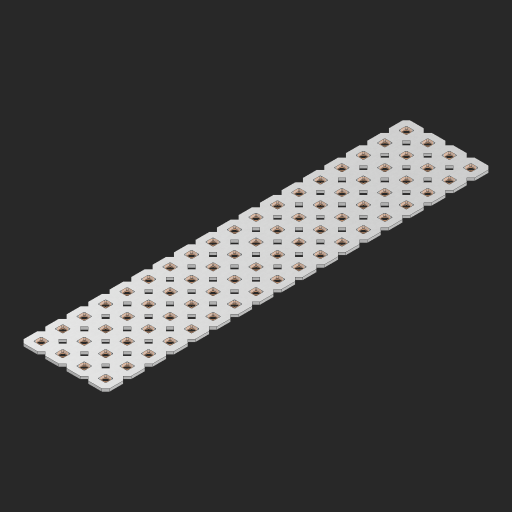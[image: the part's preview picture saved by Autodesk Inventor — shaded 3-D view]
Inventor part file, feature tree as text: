
AUTODESK INVENTOR PART (.ipt)
format: ipt  version: 2023 (Build 270158000, 158)  size: 1,118,720 bytes
history: native  units: in
note: dims shown in document units (in); Inventor stores cm internally (conversion verified against a paired STEP export)
features: other x73, extrude x71, sketch x2, pattern_linear x1
ambient origin geometry x8: Origin, YZ Plane, XZ Plane, XY Plane, X Axis, Y Axis, Z Axis, Center Point
bodies: Solid1 (feature_tree), Body (feature_tree)
feature tree (147):
  pattern_linear  "Rectangular Pattern1"  Spacing1=0.09in  [1 undecoded]
  sketch  "Sketch1"  dims[d1=0.5in]
  sketch  "Sketch2"  dims[d2=0.182in d3=0.09in d4=0.09in d5=0.09in d6=0.09in d7=0.09in d8=0.09in d9=0.09in d10=0.09in d11=0.02in d13=0.0in d14=0.172in d15=0.0625in d16=0.0in d19=0.5in d22=0.5in]
  other  "Srf1"
  other  "Srf126"
  other  "Srf127"
  other  "Srf128"
  other  "Srf129"
  other  "Srf130"
  other  "Srf131"
  other  "Srf250"
  other  "Srf251"
  other  "Srf252"
  other  "Srf253"
  other  "Srf254"
  other  "Srf255"
  other  "Srf256"
  other  "Srf257"
  other  "Srf258"
  other  "Srf259"
  other  "Srf260"
  other  "Srf268"
  other  "Srf269"
  other  "Srf270"
  other  "Srf271"
  other  "Srf272"
  other  "Srf273"
  other  "Srf274"
  other  "Srf275"
  other  "Srf276"
  other  "Srf277"
  other  "Srf278"
  other  "Srf279"
  other  "Srf280"
  other  "Srf281"
  other  "Srf282"
  other  "Srf283"
  other  "Srf284"
  other  "Srf285"
  other  "Srf293"
  other  "Srf294"
  other  "Srf295"
  other  "Srf296"
  other  "Srf297"
  other  "Srf298"
  other  "Srf299"
  other  "Srf300"
  other  "Srf301"
  other  "Srf302"
  other  "Srf303"
  other  "Srf304"
  other  "Srf305"
  other  "Srf306"
  other  "Srf307"
  other  "Srf308"
  other  "Srf309"
  other  "Srf310"
  other  "Srf318"
  other  "Srf319"
  other  "Srf320"
  other  "Srf321"
  other  "Srf322"
  other  "Srf323"
  other  "Srf324"
  other  "Srf325"
  other  "Srf326"
  other  "Srf327"
  other  "Srf328"
  other  "Srf329"
  other  "Srf330"
  other  "Srf331"
  other  "Srf332"
  other  "Srf333"
  other  "Srf334"
  other  "Srf335"
  other  "Circle"
  extrude  "ExtrusionSrf126"  Depth=0.09in
  extrude  "ExtrusionSrf127"  Depth=0.09in
  extrude  "ExtrusionSrf128"  Depth=0.09in
  extrude  "ExtrusionSrf129"  Depth=0.09in
  extrude  "ExtrusionSrf130"  Depth=0.09in
  extrude  "ExtrusionSrf131"  Depth=0.09in
  extrude  "ExtrusionSrf250"  Depth=0.09in
  extrude  "ExtrusionSrf251"  Depth=0.02in
  extrude  "ExtrusionSrf252"  TaperAngle=0.0deg  [1 undecoded]
  extrude  "ExtrusionSrf253"  Depth=0.5in
  extrude  "ExtrusionSrf254"  Depth=0.0625in TaperAngle=0.0deg
  extrude  "ExtrusionSrf255"  Depth=0.5in
  extrude  "ExtrusionSrf256"  Depth=0.5in
  extrude  "ExtrusionSrf257"  [1 undecoded]
  extrude  "ExtrusionSrf258"  [1 undecoded]
  extrude  "ExtrusionSrf259"  [1 undecoded]
  extrude  "ExtrusionSrf260"  [1 undecoded]
  extrude  "ExtrusionSrf268"  [1 undecoded]
  extrude  "ExtrusionSrf269"  [1 undecoded]
  extrude  "ExtrusionSrf270"  [1 undecoded]
  extrude  "ExtrusionSrf271"  [1 undecoded]
  extrude  "ExtrusionSrf272"  [1 undecoded]
  extrude  "ExtrusionSrf273"  [1 undecoded]
  extrude  "ExtrusionSrf274"  [1 undecoded]
  extrude  "ExtrusionSrf275"  [1 undecoded]
  extrude  "ExtrusionSrf276"  [1 undecoded]
  extrude  "ExtrusionSrf277"  [1 undecoded]
  extrude  "ExtrusionSrf278"  [1 undecoded]
  extrude  "ExtrusionSrf279"  [1 undecoded]
  extrude  "ExtrusionSrf280"  [1 undecoded]
  extrude  "ExtrusionSrf281"  [1 undecoded]
  extrude  "ExtrusionSrf282"  [1 undecoded]
  extrude  "ExtrusionSrf283"  [1 undecoded]
  extrude  "ExtrusionSrf284"  [1 undecoded]
  extrude  "ExtrusionSrf285"  [1 undecoded]
  extrude  "ExtrusionSrf293"  [1 undecoded]
  extrude  "ExtrusionSrf294"  [1 undecoded]
  extrude  "ExtrusionSrf295"  [1 undecoded]
  extrude  "ExtrusionSrf296"  [1 undecoded]
  extrude  "ExtrusionSrf297"  [1 undecoded]
  extrude  "ExtrusionSrf298"  [1 undecoded]
  extrude  "ExtrusionSrf299"  [1 undecoded]
  extrude  "ExtrusionSrf300"  [1 undecoded]
  extrude  "ExtrusionSrf301"  [1 undecoded]
  extrude  "ExtrusionSrf302"  [1 undecoded]
  extrude  "ExtrusionSrf303"  [1 undecoded]
  extrude  "ExtrusionSrf304"  [1 undecoded]
  extrude  "ExtrusionSrf305"  [1 undecoded]
  extrude  "ExtrusionSrf306"  [1 undecoded]
  extrude  "ExtrusionSrf307"  [1 undecoded]
  extrude  "ExtrusionSrf308"  [1 undecoded]
  extrude  "ExtrusionSrf309"  [1 undecoded]
  extrude  "ExtrusionSrf310"  [1 undecoded]
  extrude  "ExtrusionSrf318"  [1 undecoded]
  extrude  "ExtrusionSrf319"  [1 undecoded]
  extrude  "ExtrusionSrf320"  [1 undecoded]
  extrude  "ExtrusionSrf321"  [1 undecoded]
  extrude  "ExtrusionSrf322"  [1 undecoded]
  extrude  "ExtrusionSrf323"  [1 undecoded]
  extrude  "ExtrusionSrf324"  [1 undecoded]
  extrude  "ExtrusionSrf325"  [1 undecoded]
  extrude  "ExtrusionSrf326"  [1 undecoded]
  extrude  "ExtrusionSrf327"  [1 undecoded]
  extrude  "ExtrusionSrf328"  [1 undecoded]
  extrude  "ExtrusionSrf329"  [1 undecoded]
  extrude  "ExtrusionSrf330"  [1 undecoded]
  extrude  "ExtrusionSrf331"  [1 undecoded]
  extrude  "ExtrusionSrf332"  [1 undecoded]
  extrude  "ExtrusionSrf333"  [1 undecoded]
  extrude  "ExtrusionSrf334"  [1 undecoded]
  extrude  "ExtrusionSrf335"  [1 undecoded]
note: 60 required parameter values undecoded (feature->parameter linkage not recoverable at this tier; creation-order binding heuristic only, values carry confidence <= 0.55)
